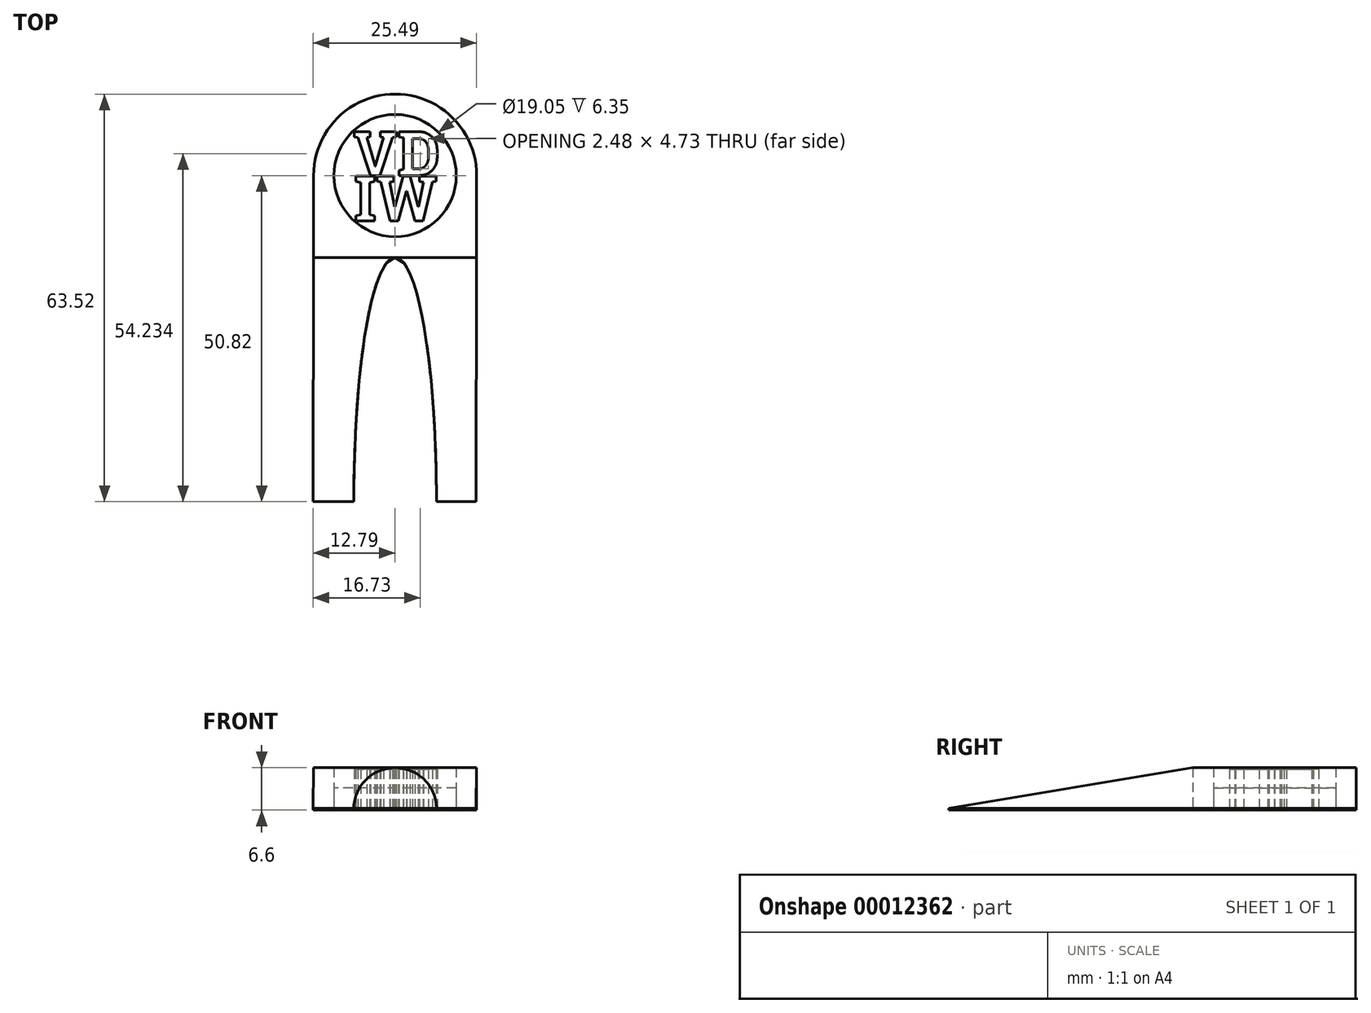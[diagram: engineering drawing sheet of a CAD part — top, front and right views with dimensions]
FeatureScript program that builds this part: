
annotation { "Feature Type Name" : "Feature", "Feature Type Description" : "" }
export const myFeature = defineFeature(function(context is Context, id is Id, definition is map)
    precondition{}
    {
        {
            var Q0;
            Q0=qCreatedBy(makeId("Top.planeOp"),FACE);
            var sketch = newSketch(context, id + "F0", { "sketchPlane" : qUnion([Q0])});
            skArc(sketch, "E0", {"start": v(12.7, -0.02) * mm, "mid": v(0.01, 12.7) * mm, "end": v(-12.7, 0) * mm});
            skLineSegment(sketch, "E1.left", {"start": v(-12.7, 0) * mm, "end": v(-12.79, -50.8) * mm});
            skLineSegment(sketch, "E1.right", {"start": v(12.7, -0.02) * mm, "end": v(12.61, -50.82) * mm});
            skLineSegment(sketch, "E2.0", {"start": v(-12.79, -50.8) * mm, "end": v(-6.44, -50.8) * mm});
            skCircle(sketch, "E3", {"center": v(0, 0) * mm, "radius": 12.7 * mm});
            skPoint(sketch, "E3.second.point", {"position": v(0.01, 12.7) * mm});
            skLineSegment(sketch, "E4.0", {"start": v(-15.96, -50.6) * mm, "end": v(-15.96, -50.82) * mm});
            skLineSegment(sketch, "E5.trimOffspring", {"start": v(15.79, -50.82) * mm, "end": v(15.79, -50.83) * mm});
            skLineSegment(sketch, "E6.trimOffspring", {"start": v(6.26, -50.82) * mm, "end": v(12.61, -50.82) * mm});
            skCircle(sketch, "E7.0", {"center": v(0, 0) * mm, "radius": 9.53 * mm});
            skLineSegment(sketch, "E8", {"start": v(0, 0) * mm, "end": v(0, -12.79) * mm});
            skEllipticalArc(sketch, "E9", {});
            skText(sketch, "E10", { "text": "VD", "fontName": "RobotoSlab-Bold.ttf"});
            skText(sketch, "E11", { "text": "IW", "fontName": "RobotoSlab-Bold.ttf"});
            const initialGuessF0  = {"E9": [0, -0.05069532385659177, 0, 1, 0.03790797373769106, 0.006437097886029921, 4.709195026903625, 1.5736992374698529], "E10": [-0.00655, 0, 1, 0, 0.00692], "E11": [-0.00637, -0.00708, 1, 0, 0.00708]};
            skSetInitialGuess(sketch, initialGuessF0);
            skSolve(sketch);
        }
        {
            var Q0;
            Q0=makeQuery(id+"F0.imprint","IMPRINT",FACE,{"disambiguationData":[TD([[makeQuery(id+"F0.imprint","IMPRINT",EDGE,{"derivedFrom":sQuery(id+"F0.wireOp",EDGE,"E7.0")}),-1.0]])]});
            extrude(context, id + "F1", {"entities" : qUnion([Q0]), "depth" : 6.35 * mm});
        }
        {
            var Q0;
            Q0=makeQuery(id+"F0.imprint","IMPRINT",FACE,{"disambiguationData":[TD([[makeQuery(id+"F0.imprint","IMPRINT",EDGE,{"derivedFrom":sQuery(id+"F0.wireOp",EDGE,"E7.0")}),1.0]])]});
            var Q1;
            Q1=makeQuery(id+"F0.imprint","IMPRINT",FACE,{"disambiguationData":[TD([[makeQuery(id+"F0.imprint","IMPRINT",EDGE,{"derivedFrom":sQuery(id+"F0.wireOp",EDGE,"E10.sketch_text.stroke-0")}),-1.0]])]});
            var Q2;
            Q2=makeQuery(id+"F0.imprint","IMPRINT",FACE,{"disambiguationData":[TD([[makeQuery(id+"F0.imprint","IMPRINT",EDGE,{"derivedFrom":sQuery(id+"F0.wireOp",EDGE,"E10.sketch_text.stroke-18")}),-1.0]])]});
            var Q3;
            Q3=makeQuery(id+"F0.imprint","IMPRINT",FACE,{"disambiguationData":[TD([[makeQuery(id+"F0.imprint","IMPRINT",EDGE,{"derivedFrom":sQuery(id+"F0.wireOp",EDGE,"E11.sketch_text.stroke-0")}),-1.0]])]});
            var Q4;
            {var subQ4=sQuery(id+"F0.wireOp",EDGE,"E11.sketch_text.stroke-19");Q4=makeQuery(id+"F0.imprint","IMPRINT",FACE,{"disambiguationData":[TD([[makeQuery(id+"F0.imprint","IMPRINT",EDGE,{"derivedFrom":subQ4}),-1.0]])]});}
            var Q5;
            Q5=makeQuery(id+"F0.imprint","IMPRINT",FACE,{"disambiguationData":[TD([[makeQuery(id+"F0.imprint","IMPRINT",EDGE,{"derivedFrom":sQuery(id+"F0.wireOp",EDGE,"E11.sketch_text.stroke-12")}),-1.0]])]});
            var Q6;
            Q6=makeQuery(id+"F0.imprint","IMPRINT",FACE,{"disambiguationData":[TD([[makeQuery(id+"F0.imprint","IMPRINT",EDGE,{"derivedFrom":sQuery(id+"F0.wireOp",EDGE,"E10.sketch_text.stroke-31")}),1.0]])]});
            extrude(context, id + "F2", {"entities" : qUnion([Q0, Q1, Q2, Q3, Q4, Q5, Q6]), "depth" : 3.17 * mm});
        }
        {
            var Q0;
            Q0=makeQuery(id+"F0.imprint","IMPRINT",FACE,{"disambiguationData":[TD([[makeQuery(id+"F0.imprint","IMPRINT",EDGE,{"derivedFrom":sQuery(id+"F0.wireOp",EDGE,"E7.0")}),1.0]])]});
            var Q1;
            Q1=makeQuery(id+"F0.imprint","IMPRINT",FACE,{"disambiguationData":[TD([[makeQuery(id+"F0.imprint","IMPRINT",EDGE,{"derivedFrom":sQuery(id+"F0.wireOp",EDGE,"e0804143-4723-42b6-951f-b85cdecca350.sketch_text.stroke-13")}),1.0]])]});
            var Q2;
            Q2=makeQuery(id+"F0.imprint","IMPRINT",FACE,{"disambiguationData":[TD([[makeQuery(id+"F0.imprint","IMPRINT",EDGE,{"derivedFrom":sQuery(id+"F0.wireOp",EDGE,"E10.sketch_text.stroke-18")}),-1.0]])]});
            var Q3;
            Q3=makeQuery(id+"F0.imprint","IMPRINT",FACE,{"disambiguationData":[TD([[makeQuery(id+"F0.imprint","IMPRINT",EDGE,{"derivedFrom":sQuery(id+"F0.wireOp",EDGE,"E10.sketch_text.stroke-31")}),1.0]])]});
            var Q4;
            Q4=makeQuery(id+"F0.imprint","IMPRINT",FACE,{"disambiguationData":[TD([[makeQuery(id+"F0.imprint","IMPRINT",EDGE,{"derivedFrom":sQuery(id+"F0.wireOp",EDGE,"E11.sketch_text.stroke-12")}),-1.0]])]});
            var Q5;
            {var subQ4=sQuery(id+"F0.wireOp",EDGE,"E11.sketch_text.stroke-19");Q5=makeQuery(id+"F0.imprint","IMPRINT",FACE,{"disambiguationData":[TD([[makeQuery(id+"F0.imprint","IMPRINT",EDGE,{"derivedFrom":subQ4}),-1.0]])]});}
            var Q6;
            Q6=makeQuery(id+"F0.imprint","IMPRINT",FACE,{"disambiguationData":[TD([[makeQuery(id+"F0.imprint","IMPRINT",EDGE,{"derivedFrom":sQuery(id+"F0.wireOp",EDGE,"E10.sketch_text.stroke-0")}),-1.0]])]});
            var Q7;
            Q7=makeQuery(id+"F0.imprint","IMPRINT",FACE,{"disambiguationData":[TD([[makeQuery(id+"F0.imprint","IMPRINT",EDGE,{"derivedFrom":sQuery(id+"F0.wireOp",EDGE,"E11.sketch_text.stroke-0")}),-1.0]])]});
            extrude(context, id + "F3", {"entities" : qUnion([Q0, Q1, Q2, Q3, Q4, Q5, Q6, Q7]), "depth" : 3.17 * mm});
        }
        {
            var Q0;
            {var subQ6=sQuery(id+"F0.wireOp",EDGE,"E1.left");Q0=makeQuery(id+"F0.imprint","IMPRINT",FACE,{"disambiguationData":[TD([[makeQuery(id+"F0.imprint","IMPRINT",EDGE,{"derivedFrom":subQ6}),1.0]])]});}
            var Q1;
            {var subQ7=sQuery(id+"F0.wireOp",EDGE,"E1.right");Q1=makeQuery(id+"F0.imprint","IMPRINT",FACE,{"disambiguationData":[TD([[makeQuery(id+"F0.imprint","IMPRINT",EDGE,{"derivedFrom":subQ7}),-1.0]])]});}
            var Q2;
            Q2=makeQuery(id+"F1.opExtrude","SWEPT_BODY",BODY,{"disambiguationData":[OSD([sQuery(id+"F0.wireOp",EDGE,"E3"),sQuery(id+"F0.wireOp",EDGE,"E7.0")])]});
            extrude(context, id + "F4", {"entities" : qUnion([Q0, Q1]), "operationType" : NewBodyOperationType.ADD, "endBoundEntity" : qUnion([Q2]), "depth" : 6.35 * mm});
        }
        {
            var Q0;
            Q0=makeQuery(id+"F0.imprint","IMPRINT",FACE,{"disambiguationData":[TD([[makeQuery(id+"F0.imprint","IMPRINT",EDGE,{"derivedFrom":sQuery(id+"F0.wireOp",EDGE,"E10.sketch_text.stroke-0")}),-1.0]])]});
            var Q1;
            Q1=makeQuery(id+"F0.imprint","IMPRINT",FACE,{"disambiguationData":[TD([[makeQuery(id+"F0.imprint","IMPRINT",EDGE,{"derivedFrom":sQuery(id+"F0.wireOp",EDGE,"E10.sketch_text.stroke-18")}),-1.0]])]});
            var Q2;
            Q2=makeQuery(id+"F0.imprint","IMPRINT",FACE,{"disambiguationData":[TD([[makeQuery(id+"F0.imprint","IMPRINT",EDGE,{"derivedFrom":sQuery(id+"F0.wireOp",EDGE,"E11.sketch_text.stroke-0")}),-1.0]])]});
            var Q3;
            {var subQ4=sQuery(id+"F0.wireOp",EDGE,"E11.sketch_text.stroke-19");Q3=makeQuery(id+"F0.imprint","IMPRINT",FACE,{"disambiguationData":[TD([[makeQuery(id+"F0.imprint","IMPRINT",EDGE,{"derivedFrom":subQ4}),-1.0]])]});}
            var Q4;
            Q4=makeQuery(id+"F0.imprint","IMPRINT",FACE,{"disambiguationData":[TD([[makeQuery(id+"F0.imprint","IMPRINT",EDGE,{"derivedFrom":sQuery(id+"F0.wireOp",EDGE,"E11.sketch_text.stroke-12")}),-1.0]])]});
            extrude(context, id + "F5", {"entities" : qUnion([Q0, Q1, Q2, Q3, Q4]), "depth" : 6.1 * mm});
        }
        {
            var Q0;
            Q0=makeQuery(id+"F4.opExtrude","SWEPT_FACE",FACE,{"disambiguationData":[OSD([sQuery(id+"F0.wireOp",EDGE,"E1.left")])]});
            var sketch = newSketch(context, id + "F6", { "sketchPlane" : qUnion([Q0])});
            skLineSegment(sketch, "E12", {"start": v(12.79, 0) * mm, "end": v(12.79, 6.35) * mm});
            skLineSegment(sketch, "E13", {"start": v(12.79, 6.35) * mm, "end": v(50.82, 6.35) * mm});
            skLineSegment(sketch, "E14", {"start": v(50.82, 6.35) * mm, "end": v(50.82, 0) * mm});
            skLineSegment(sketch, "E15", {"start": v(50.82, 0) * mm, "end": v(12.79, 6.35) * mm});
            skSolve(sketch);
        }
        {
            var Q0;
            Q0=makeQuery(id+"F6.imprint","IMPRINT",FACE,{"disambiguationData":[TD([[makeQuery(id+"F6.imprint","IMPRINT",EDGE,{"derivedFrom":sQuery(id+"F6.wireOp",EDGE,"E13")}),-1.0]])]});
            extrude(context, id + "F7", {"entities" : qUnion([Q0]), "operationType" : NewBodyOperationType.REMOVE, "endBound" : BoundingType.THROUGH_ALL, "oppositeDirection" : true, "depth" : 25.4 * mm});
        }
        {
            var Q0;
            {var subQ6=sQuery(id+"F0.wireOp",EDGE,"E1.left");Q0=makeQuery(id+"F0.imprint","IMPRINT",FACE,{"disambiguationData":[TD([[makeQuery(id+"F0.imprint","IMPRINT",EDGE,{"derivedFrom":subQ6}),1.0]])]});}
            var Q1;
            {var subQ7=sQuery(id+"F0.wireOp",EDGE,"E1.right");Q1=makeQuery(id+"F0.imprint","IMPRINT",FACE,{"disambiguationData":[TD([[makeQuery(id+"F0.imprint","IMPRINT",EDGE,{"derivedFrom":subQ7}),-1.0]])]});}
            var Q2;
            Q2=makeQuery(id+"F0.imprint","IMPRINT",FACE,{"disambiguationData":[TD([[makeQuery(id+"F0.imprint","IMPRINT",EDGE,{"derivedFrom":sQuery(id+"F0.wireOp",EDGE,"E7.0")}),-1.0]])]});
            var Q3;
            Q3=makeQuery(id+"F0.imprint","IMPRINT",FACE,{"disambiguationData":[TD([[makeQuery(id+"F0.imprint","IMPRINT",EDGE,{"derivedFrom":sQuery(id+"F0.wireOp",EDGE,"E7.0")}),1.0]])]});
            var Q4;
            Q4=makeQuery(id+"F0.imprint","IMPRINT",FACE,{"disambiguationData":[TD([[makeQuery(id+"F0.imprint","IMPRINT",EDGE,{"derivedFrom":sQuery(id+"F0.wireOp",EDGE,"E11.sketch_text.stroke-0")}),-1.0]])]});
            var Q5;
            {var subQ4=sQuery(id+"F0.wireOp",EDGE,"E11.sketch_text.stroke-19");Q5=makeQuery(id+"F0.imprint","IMPRINT",FACE,{"disambiguationData":[TD([[makeQuery(id+"F0.imprint","IMPRINT",EDGE,{"derivedFrom":subQ4}),-1.0]])]});}
            var Q6;
            Q6=makeQuery(id+"F0.imprint","IMPRINT",FACE,{"disambiguationData":[TD([[makeQuery(id+"F0.imprint","IMPRINT",EDGE,{"derivedFrom":sQuery(id+"F0.wireOp",EDGE,"E11.sketch_text.stroke-12")}),-1.0]])]});
            var Q7;
            Q7=makeQuery(id+"F0.imprint","IMPRINT",FACE,{"disambiguationData":[TD([[makeQuery(id+"F0.imprint","IMPRINT",EDGE,{"derivedFrom":sQuery(id+"F0.wireOp",EDGE,"E10.sketch_text.stroke-0")}),-1.0]])]});
            var Q8;
            Q8=makeQuery(id+"F0.imprint","IMPRINT",FACE,{"disambiguationData":[TD([[makeQuery(id+"F0.imprint","IMPRINT",EDGE,{"derivedFrom":sQuery(id+"F0.wireOp",EDGE,"E10.sketch_text.stroke-18")}),-1.0]])]});
            var Q9;
            Q9=makeQuery(id+"F0.imprint","IMPRINT",FACE,{"disambiguationData":[TD([[makeQuery(id+"F0.imprint","IMPRINT",EDGE,{"derivedFrom":sQuery(id+"F0.wireOp",EDGE,"E10.sketch_text.stroke-31")}),1.0]])]});
            extrude(context, id + "F8", {"entities" : qUnion([Q0, Q1, Q2, Q3, Q4, Q5, Q6, Q7, Q8, Q9]), "oppositeDirection" : true, "depth" : 0.25 * mm});
        }
    });
